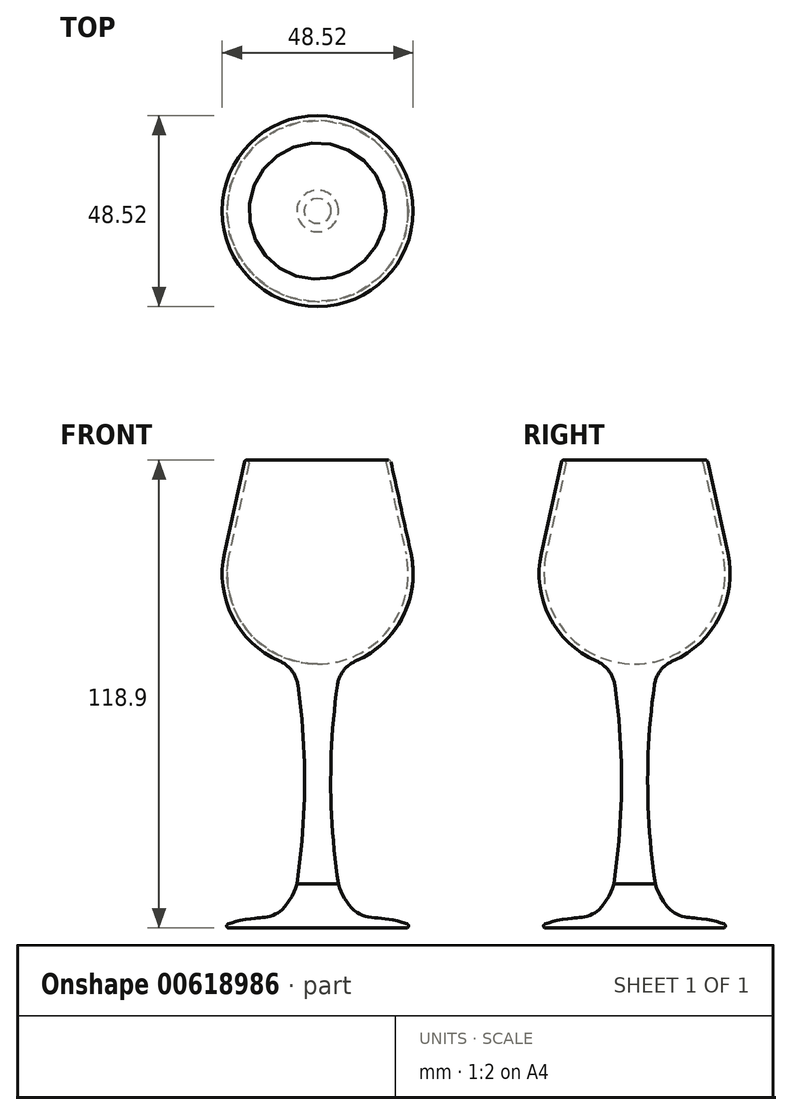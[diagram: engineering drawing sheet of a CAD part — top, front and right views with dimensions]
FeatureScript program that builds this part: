
annotation { "Feature Type Name" : "Feature", "Feature Type Description" : "" }
export const myFeature = defineFeature(function(context is Context, id is Id, definition is map)
    precondition{}
    {
        {
            var Q0;
            Q0=qCreatedBy(makeId("Front.planeOp"),FACE);
            var sketch = newSketch(context, id + "F0", { "sketchPlane" : qUnion([Q0])});
            skArc(sketch, "E0", {"start": v(-5.28, -50.54) * mm, "mid": v(-3.33, -25.28) * mm, "end": v(-5.02, 0) * mm});
            skArc(sketch, "E1", {"start": v(-23.7, 33.58) * mm, "mid": v(-21.6, 17.34) * mm, "end": v(-9.68, 6.13) * mm});
            skLineSegment(sketch, "E2", {"start": v(-23.7, 33.58) * mm, "end": v(-18.62, 56.71) * mm});
            skArc(sketch, "E3", {"start": v(-5.02, 0) * mm, "mid": v(-6.55, 3.67) * mm, "end": v(-9.68, 6.13) * mm});
            skFitSpline(sketch, "E4", {"points": [v(-5.28, -50.54) * mm, v(-9.46, -57.35) * mm, v(-14.39, -59.08) * mm, v(-25.1, -61.7) * mm], "startDerivative": vector(-6.18, -21.9) * mm, "endDerivative": vector(-37.5, -17.65) * mm});
            skLineSegment(sketch, "E5", {"start": v(-22.6, -61.7) * mm, "end": v(0, -61.7) * mm});
            skArc(sketch, "E6.filletArc", {"start": v(-22.77, -60.7) * mm, "mid": v(-23.1, -61.27) * mm, "end": v(-22.6, -61.7) * mm});
            skLineSegment(sketch, "E7.0", {"start": v(-22.46, 33.3) * mm, "end": v(-17.38, 56.44) * mm});
            skArc(sketch, "E7.1", {"start": v(-22.46, 33.3) * mm, "mid": v(-17.92, 13.96) * mm, "end": v(0, 5.38) * mm});
            skLineSegment(sketch, "E8", {"start": v(-17.5, 56.97) * mm, "end": v(-17.5, 56.97) * mm});
            skPoint(sketch, "E9.visualSharp", {"position": v(-18.33, 58.03) * mm});
            skArc(sketch, "E9.filletArc", {"start": v(-17.5, 56.97) * mm, "mid": v(-18.14, 57.2) * mm, "end": v(-18.62, 56.71) * mm});
            skPoint(sketch, "E10.visualSharp", {"position": v(-17.32, 56.73) * mm});
            skArc(sketch, "E10.filletArc", {"start": v(-17.38, 56.44) * mm, "mid": v(-17.38, 56.72) * mm, "end": v(-17.5, 56.97) * mm});
            skLineSegment(sketch, "E11", {"start": v(0, 78.42) * mm, "end": v(0, -74.74) * mm});
            skSolve(sketch);
        }
        {
            var Q0;
            Q0=makeQuery(id+"F0.imprint","IMPRINT",FACE,{"disambiguationData":[TD([[makeQuery(id+"F0.imprint","IMPRINT",EDGE,{"derivedFrom":sQuery(id+"F0.wireOp",EDGE,"E0")}),-1.0]])]});
            var Q1;
            Q1=sQuery(id+"F0.wireOp",EDGE,"E11");
            revolve(context, id + "F1", {"entities" : qUnion([Q0]), "axis" : qUnion([Q1]), "revolveType" : RevolveType.FULL});
        }
    });
